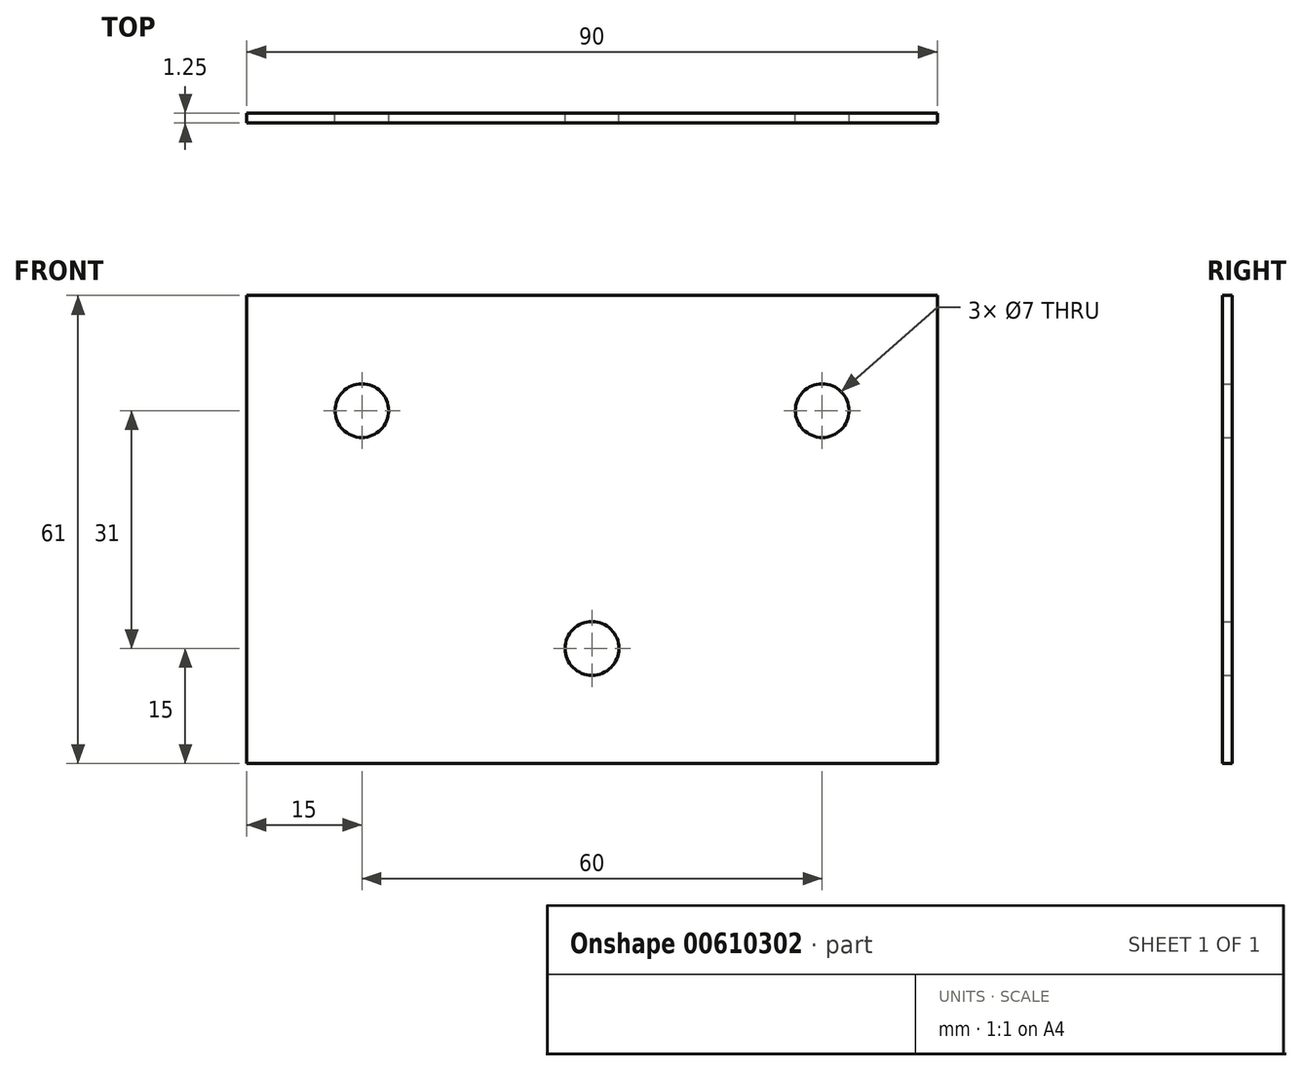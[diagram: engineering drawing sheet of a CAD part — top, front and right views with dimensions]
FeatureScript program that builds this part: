
annotation { "Feature Type Name" : "Feature", "Feature Type Description" : "" }
export const myFeature = defineFeature(function(context is Context, id is Id, definition is map)
    precondition{}
    {
        {
            var Q0;
            Q0=qCreatedBy(makeId("Front.planeOp"),FACE);
            var sketch = newSketch(context, id + "F0", { "sketchPlane" : qUnion([Q0])});
            skLineSegment(sketch, "E0.bottom", {"start": v(-45, 30.5) * mm, "end": v(45, 30.5) * mm});
            skLineSegment(sketch, "E0.top", {"start": v(-45, -30.5) * mm, "end": v(45, -30.5) * mm});
            skLineSegment(sketch, "E0.left", {"start": v(-45, 30.5) * mm, "end": v(-45, -30.5) * mm});
            skLineSegment(sketch, "E0.right", {"start": v(45, 30.5) * mm, "end": v(45, -30.5) * mm});
            skLineSegment(sketch, "E1", {"start": v(0, 0) * mm, "end": v(0, 30.5) * mm, "construction": true});
            skLineSegment(sketch, "E2", {"start": v(0, 0) * mm, "end": v(-45, 0) * mm, "construction": true});
            skCircle(sketch, "E3", {"center": v(0, -15.5) * mm, "radius": 3.5 * mm});
            skCircle(sketch, "E4", {"center": v(30, 15.5) * mm, "radius": 3.5 * mm});
            skCircle(sketch, "E5", {"center": v(-30, 15.5) * mm, "radius": 3.5 * mm});
            skLineSegment(sketch, "E6", {"start": v(-30, 15.5) * mm, "end": v(30, 15.5) * mm, "construction": true});
            skLineSegment(sketch, "E7", {"start": v(0, -15.5) * mm, "end": v(0, 0) * mm, "construction": true});
            skLineSegment(sketch, "E8", {"start": v(-30, 15.5) * mm, "end": v(-45, 15.5) * mm});
            skLineSegment(sketch, "E9", {"start": v(-45, 15.5) * mm, "end": v(-30, 15.5) * mm});
            skLineSegment(sketch, "E10", {"start": v(-30, 30.5) * mm, "end": v(-30, 15.5) * mm});
            skLineSegment(sketch, "E11", {"start": v(30, 15.5) * mm, "end": v(45, 15.5) * mm});
            skLineSegment(sketch, "E12", {"start": v(30, 15.5) * mm, "end": v(30, 30.5) * mm});
            skLineSegment(sketch, "E13", {"start": v(0, -15.5) * mm, "end": v(0, -30.5) * mm});
            skSolve(sketch);
        }
        {
            var Q0;
            Q0=makeQuery(id+"F0.imprint","IMPRINT",FACE,{"disambiguationData":[TD([[makeQuery(id+"F0.imprint","IMPRINT",EDGE,{"derivedFrom":sQuery(id+"F0.wireOp",EDGE,"E3")}),-1.0]])]});
            var Q1;
            {var subQ1=sQuery(id+"F0.wireOp",EDGE,"E0.left");var subQ7=sQuery(id+"F0.wireOp",EDGE,"E0.bottom");var subQ8=makeQuery(id+"F0.imprint","INTERSECT",VERTEX,{"derivedFrom":[subQ7,subQ1]});Q1=makeQuery(id+"F0.imprint","IMPRINT",FACE,{"disambiguationData":[TD([[makeQuery(id+"F0.imprint","IMPRINT",EDGE,{"disambiguationData":[TD([[subQ8,-1.0]])],"derivedFrom":subQ7}),-1.0]])]});}
            var Q2;
            {var subQ1=sQuery(id+"F0.wireOp",EDGE,"E0.right");var subQ7=sQuery(id+"F0.wireOp",EDGE,"E0.bottom");var subQ9=makeQuery(id+"F0.imprint","INTERSECT",VERTEX,{"derivedFrom":[subQ7,subQ1]});Q2=makeQuery(id+"F0.imprint","IMPRINT",FACE,{"disambiguationData":[TD([[makeQuery(id+"F0.imprint","IMPRINT",EDGE,{"disambiguationData":[TD([[subQ9,1.0]])],"derivedFrom":subQ7}),-1.0]])]});}
            extrude(context, id + "F1", {"entities" : qUnion([Q0, Q1, Q2]), "depth" : 1.25 * mm, "offsetDistance" : 25 * mm});
        }
    });
